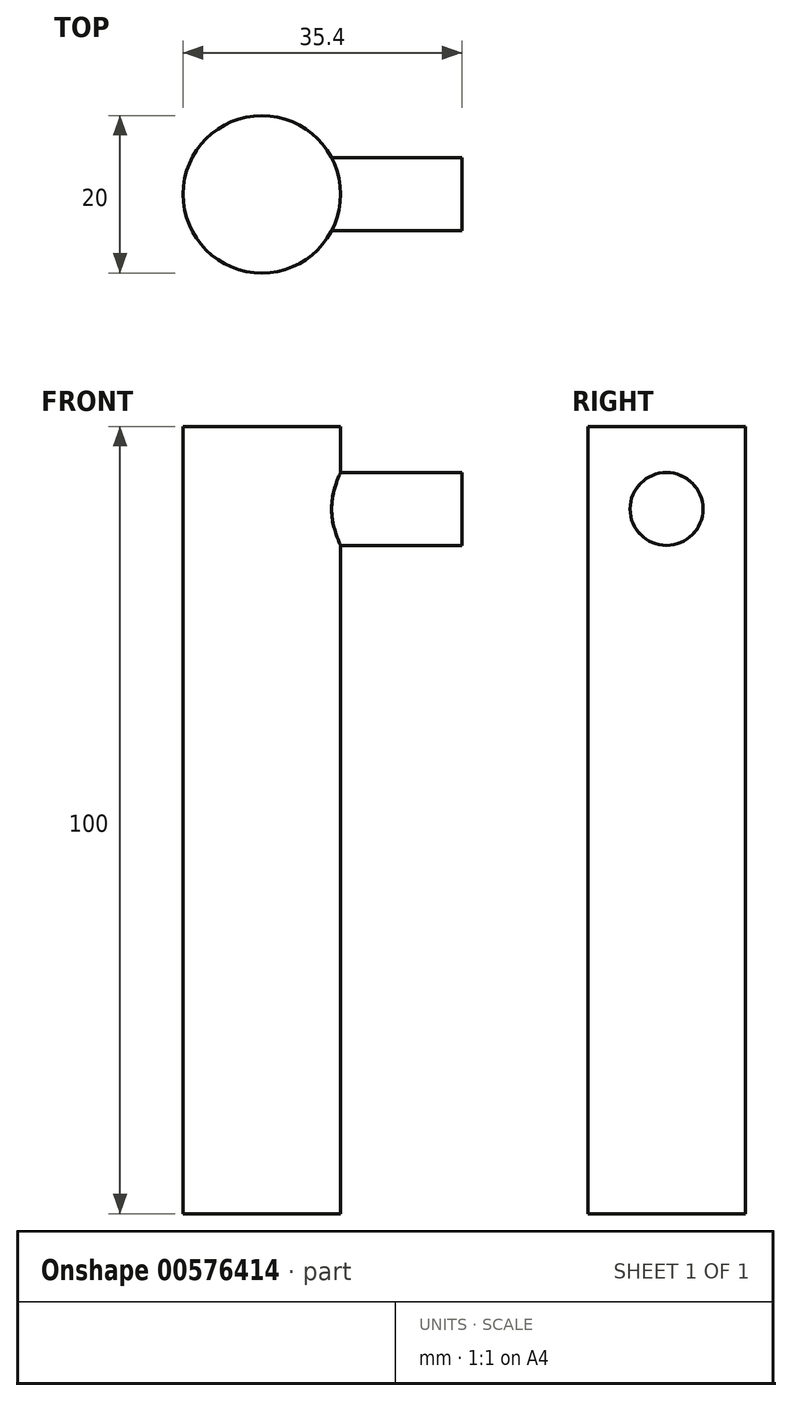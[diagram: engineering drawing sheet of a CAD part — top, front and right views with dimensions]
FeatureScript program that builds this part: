
annotation { "Feature Type Name" : "Feature", "Feature Type Description" : "" }
export const myFeature = defineFeature(function(context is Context, id is Id, definition is map)
    precondition{}
    {
        {
            var Q0;
            Q0=qCreatedBy(makeId("Top.planeOp"),FACE);
            var sketch = newSketch(context, id + "F0", { "sketchPlane" : qUnion([Q0])});
            skCircle(sketch, "E0", {"center": v(0, 0) * mm, "radius": 10 * mm});
            skSolve(sketch);
        }
        {
            var Q0;
            Q0=makeQuery(id+"F0.imprint","IMPRINT",FACE,{"disambiguationData":[TD([[makeQuery(id+"F0.imprint","IMPRINT",EDGE,{"derivedFrom":sQuery(id+"F0.wireOp",EDGE,"E0")}),1.0]])]});
            extrude(context, id + "F1", {"entities" : qUnion([Q0]), "depth" : 100 * mm, "offsetDistance" : 25.4 * mm});
        }
        {
            var Q0;
            Q0=qCreatedBy(makeId("Right.planeOp"),FACE);
            var sketch = newSketch(context, id + "F2", { "sketchPlane" : qUnion([Q0])});
            skCircle(sketch, "E1", {"center": v(0, 89.52) * mm, "radius": 4.63 * mm});
            skSolve(sketch);
        }
        {
            var Q0;
            Q0 = qSketchRegion(id + "F2", true);
            extrude(context, id + "F3", {"entities" : qUnion([Q0]), "operationType" : NewBodyOperationType.ADD, "depth" : 25.4 * mm, "offsetDistance" : 25.4 * mm});
        }
    });
